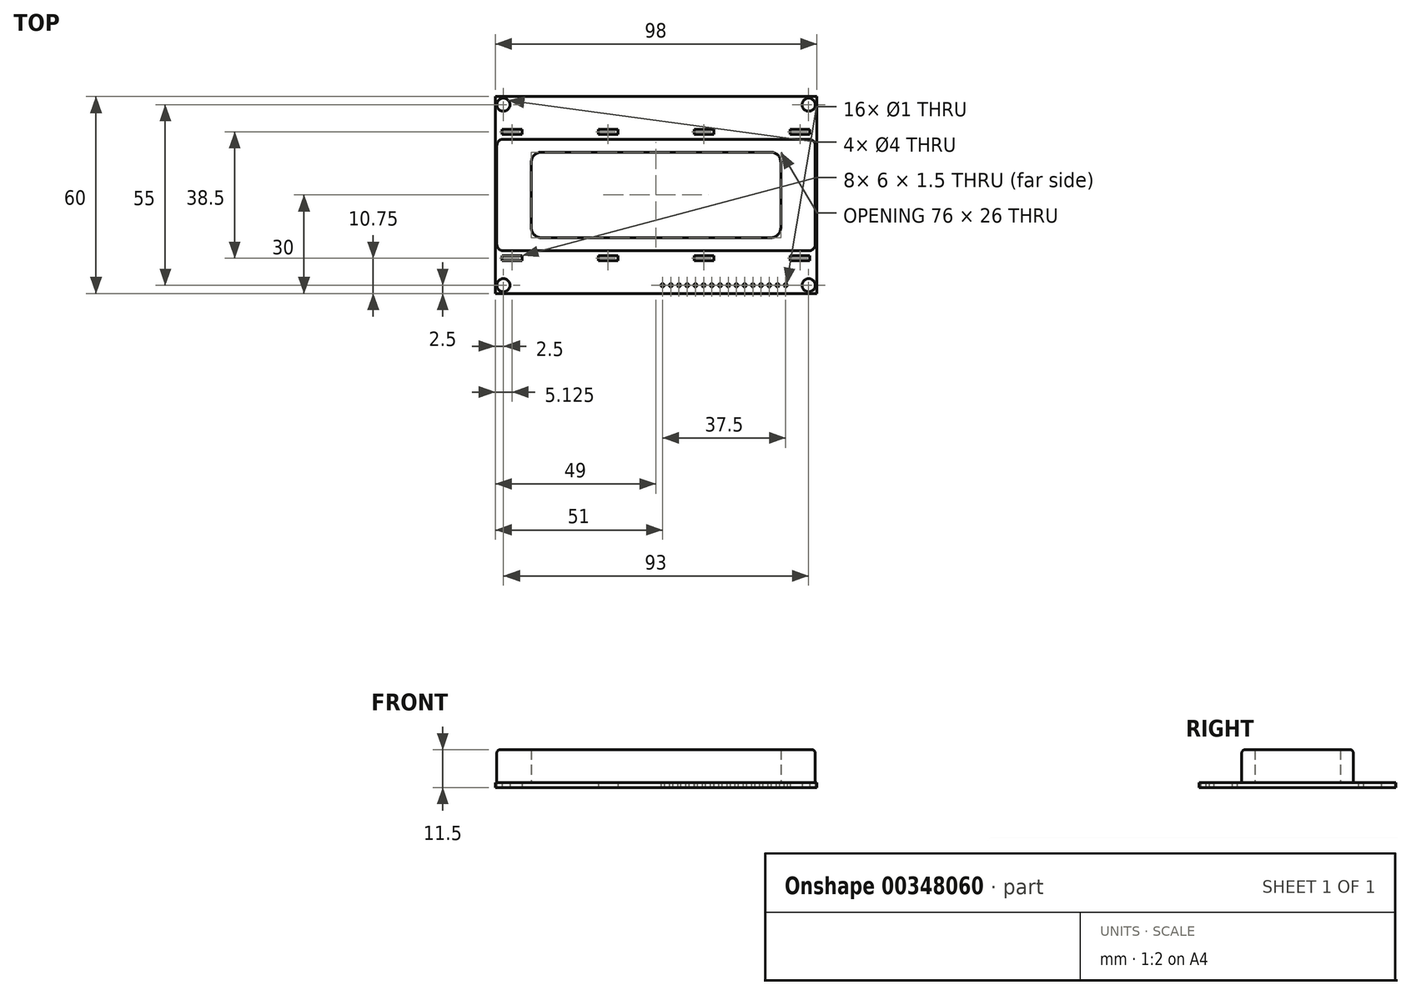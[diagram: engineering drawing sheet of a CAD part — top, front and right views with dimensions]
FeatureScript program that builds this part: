
annotation { "Feature Type Name" : "Feature", "Feature Type Description" : "" }
export const myFeature = defineFeature(function(context is Context, id is Id, definition is map)
    precondition{}
    {
        {
            var Q0;
            Q0=qCreatedBy(makeId("Top.planeOp"),FACE);
            var sketch = newSketch(context, id + "F0", { "sketchPlane" : qUnion([Q0])});
            skLineSegment(sketch, "E0.bottom", {"start": v(-49, 30) * mm, "end": v(49, 30) * mm});
            skLineSegment(sketch, "E0.top", {"start": v(-49, -30) * mm, "end": v(49, -30) * mm});
            skLineSegment(sketch, "E0.left", {"start": v(-49, 30) * mm, "end": v(-49, -30) * mm});
            skLineSegment(sketch, "E0.right", {"start": v(49, 30) * mm, "end": v(49, -30) * mm});
            skPoint(sketch, "E0.middle", {"position": v(0, 0) * mm});
            skCircle(sketch, "E1", {"center": v(-46.5, 27.5) * mm, "radius": 2 * mm});
            skCircle(sketch, "E2.MirrorC", {"center": v(46.5, 27.5) * mm, "radius": 2 * mm});
            skCircle(sketch, "E3.MirrorC", {"center": v(46.5, -27.5) * mm, "radius": 2 * mm});
            skCircle(sketch, "E4.MirrorC", {"center": v(-46.5, -27.5) * mm, "radius": 2 * mm});
            skLineSegment(sketch, "E5.bottom", {"start": v(-46.87, 20) * mm, "end": v(-40.87, 20) * mm});
            skLineSegment(sketch, "E5.top", {"start": v(-46.87, 18.5) * mm, "end": v(-40.87, 18.5) * mm});
            skLineSegment(sketch, "E5.left", {"start": v(-46.87, 20) * mm, "end": v(-46.87, 18.5) * mm});
            skLineSegment(sketch, "E5.right", {"start": v(-40.87, 20) * mm, "end": v(-40.87, 18.5) * mm});
            skLineSegment(sketch, "E6.1.0.0", {"start": v(-17.62, 18.5) * mm, "end": v(-11.62, 18.5) * mm});
            skLineSegment(sketch, "E6.1.0.1", {"start": v(-11.62, 20) * mm, "end": v(-11.62, 18.5) * mm});
            skLineSegment(sketch, "E6.1.0.2", {"start": v(-17.62, 20) * mm, "end": v(-11.62, 20) * mm});
            skLineSegment(sketch, "E6.1.0.3", {"start": v(-17.62, 20) * mm, "end": v(-17.62, 18.5) * mm});
            skLineSegment(sketch, "E6.2.0.0", {"start": v(11.63, 18.5) * mm, "end": v(17.63, 18.5) * mm});
            skLineSegment(sketch, "E6.2.0.1", {"start": v(17.63, 20) * mm, "end": v(17.63, 18.5) * mm});
            skLineSegment(sketch, "E6.2.0.2", {"start": v(11.63, 20) * mm, "end": v(17.63, 20) * mm});
            skLineSegment(sketch, "E6.2.0.3", {"start": v(11.63, 20) * mm, "end": v(11.63, 18.5) * mm});
            skLineSegment(sketch, "E6.3.0.0", {"start": v(40.88, 18.5) * mm, "end": v(46.88, 18.5) * mm});
            skLineSegment(sketch, "E6.3.0.1", {"start": v(46.88, 20) * mm, "end": v(46.88, 18.5) * mm});
            skLineSegment(sketch, "E6.3.0.2", {"start": v(40.88, 20) * mm, "end": v(46.88, 20) * mm});
            skLineSegment(sketch, "E6.3.0.3", {"start": v(40.88, 20) * mm, "end": v(40.88, 18.5) * mm});
            skLineSegment(sketch, "E6.direction1", {"start": v(-46.87, 18.5) * mm, "end": v(-17.62, 18.5) * mm, "construction": true});
            skLineSegment(sketch, "E7.MirrorCS", {"start": v(-46.87, -20) * mm, "end": v(-40.87, -20) * mm});
            skLineSegment(sketch, "E8.MirrorCS", {"start": v(-46.87, -20) * mm, "end": v(-46.87, -18.5) * mm});
            skLineSegment(sketch, "E9.MirrorCS", {"start": v(-40.87, -20) * mm, "end": v(-40.87, -18.5) * mm});
            skLineSegment(sketch, "E10", {"start": v(-46.87, -18.5) * mm, "end": v(-40.87, -18.5) * mm});
            skLineSegment(sketch, "E11.1.0.0", {"start": v(-17.62, -20) * mm, "end": v(-11.62, -20) * mm});
            skLineSegment(sketch, "E11.1.0.1", {"start": v(-17.62, -18.5) * mm, "end": v(-11.62, -18.5) * mm});
            skLineSegment(sketch, "E11.1.0.2", {"start": v(-11.62, -20) * mm, "end": v(-11.62, -18.5) * mm});
            skLineSegment(sketch, "E11.1.0.3", {"start": v(-17.62, -20) * mm, "end": v(-17.62, -18.5) * mm});
            skLineSegment(sketch, "E11.2.0.0", {"start": v(11.63, -20) * mm, "end": v(17.63, -20) * mm});
            skLineSegment(sketch, "E11.2.0.1", {"start": v(11.63, -18.5) * mm, "end": v(17.63, -18.5) * mm});
            skLineSegment(sketch, "E11.2.0.2", {"start": v(17.63, -20) * mm, "end": v(17.63, -18.5) * mm});
            skLineSegment(sketch, "E11.2.0.3", {"start": v(11.63, -20) * mm, "end": v(11.63, -18.5) * mm});
            skLineSegment(sketch, "E11.3.0.0", {"start": v(40.88, -20) * mm, "end": v(46.88, -20) * mm});
            skLineSegment(sketch, "E11.3.0.1", {"start": v(40.88, -18.5) * mm, "end": v(46.88, -18.5) * mm});
            skLineSegment(sketch, "E11.3.0.2", {"start": v(46.88, -20) * mm, "end": v(46.88, -18.5) * mm});
            skLineSegment(sketch, "E11.3.0.3", {"start": v(40.88, -20) * mm, "end": v(40.88, -18.5) * mm});
            skLineSegment(sketch, "E11.direction1", {"start": v(-46.87, -20) * mm, "end": v(-17.62, -20) * mm, "construction": true});
            skCircle(sketch, "E12", {"center": v(2, -27.5) * mm, "radius": 0.5 * mm});
            skCircle(sketch, "E13.1.0.0", {"center": v(4.5, -27.5) * mm, "radius": 0.5 * mm});
            skCircle(sketch, "E13.2.0.0", {"center": v(7, -27.5) * mm, "radius": 0.5 * mm});
            skCircle(sketch, "E13.3.0.0", {"center": v(9.5, -27.5) * mm, "radius": 0.5 * mm});
            skCircle(sketch, "E13.4.0.0", {"center": v(12, -27.5) * mm, "radius": 0.5 * mm});
            skCircle(sketch, "E13.5.0.0", {"center": v(14.5, -27.5) * mm, "radius": 0.5 * mm});
            skCircle(sketch, "E13.6.0.0", {"center": v(17, -27.5) * mm, "radius": 0.5 * mm});
            skCircle(sketch, "E13.7.0.0", {"center": v(19.5, -27.5) * mm, "radius": 0.5 * mm});
            skCircle(sketch, "E13.8.0.0", {"center": v(22, -27.5) * mm, "radius": 0.5 * mm});
            skCircle(sketch, "E13.9.0.0", {"center": v(24.5, -27.5) * mm, "radius": 0.5 * mm});
            skCircle(sketch, "E13.10.0.0", {"center": v(27, -27.5) * mm, "radius": 0.5 * mm});
            skCircle(sketch, "E13.11.0.0", {"center": v(29.5, -27.5) * mm, "radius": 0.5 * mm});
            skCircle(sketch, "E13.12.0.0", {"center": v(32, -27.5) * mm, "radius": 0.5 * mm});
            skCircle(sketch, "E13.13.0.0", {"center": v(34.5, -27.5) * mm, "radius": 0.5 * mm});
            skCircle(sketch, "E13.14.0.0", {"center": v(37, -27.5) * mm, "radius": 0.5 * mm});
            skCircle(sketch, "E13.15.0.0", {"center": v(39.5, -27.5) * mm, "radius": 0.5 * mm});
            skLineSegment(sketch, "E13.direction1", {"start": v(2, -27.5) * mm, "end": v(4.5, -27.5) * mm, "construction": true});
            skSolve(sketch);
        }
        {
            var Q0;
            Q0=makeQuery(id+"F0.imprint","IMPRINT",FACE,{"disambiguationData":[TD([[makeQuery(id+"F0.imprint","IMPRINT",EDGE,{"derivedFrom":sQuery(id+"F0.wireOp",EDGE,"E0.bottom")}),-1.0]])]});
            extrude(context, id + "F1", {"entities" : qUnion([Q0]), "depth" : 1.5 * mm});
        }
        {
            var Q0;
            Q0=makeQuery(id+"F1.opExtrude","CAP_FACE",FACE,{"disambiguationData":[OSD([sQuery(id+"F0.wireOp",EDGE,"E0.bottom"),sQuery(id+"F0.wireOp",EDGE,"E0.top"),sQuery(id+"F0.wireOp",EDGE,"E0.left"),sQuery(id+"F0.wireOp",EDGE,"E0.right"),sQuery(id+"F0.wireOp",EDGE,"E1"),sQuery(id+"F0.wireOp",EDGE,"E2.MirrorC"),sQuery(id+"F0.wireOp",EDGE,"E3.MirrorC"),sQuery(id+"F0.wireOp",EDGE,"E4.MirrorC"),sQuery(id+"F0.wireOp",EDGE,"E5.bottom"),sQuery(id+"F0.wireOp",EDGE,"E5.top"),sQuery(id+"F0.wireOp",EDGE,"E5.left"),sQuery(id+"F0.wireOp",EDGE,"E5.right"),sQuery(id+"F0.wireOp",EDGE,"E6.1.0.0"),sQuery(id+"F0.wireOp",EDGE,"E6.1.0.1"),sQuery(id+"F0.wireOp",EDGE,"E6.1.0.2"),sQuery(id+"F0.wireOp",EDGE,"E6.1.0.3"),sQuery(id+"F0.wireOp",EDGE,"E6.2.0.0"),sQuery(id+"F0.wireOp",EDGE,"E6.2.0.1"),sQuery(id+"F0.wireOp",EDGE,"E6.2.0.2"),sQuery(id+"F0.wireOp",EDGE,"E6.2.0.3"),sQuery(id+"F0.wireOp",EDGE,"E6.3.0.0"),sQuery(id+"F0.wireOp",EDGE,"E6.3.0.1"),sQuery(id+"F0.wireOp",EDGE,"E6.3.0.2"),sQuery(id+"F0.wireOp",EDGE,"E6.3.0.3"),sQuery(id+"F0.wireOp",EDGE,"E7.MirrorCS"),sQuery(id+"F0.wireOp",EDGE,"E8.MirrorCS"),sQuery(id+"F0.wireOp",EDGE,"E9.MirrorCS"),sQuery(id+"F0.wireOp",EDGE,"E10"),sQuery(id+"F0.wireOp",EDGE,"E11.1.0.0"),sQuery(id+"F0.wireOp",EDGE,"E11.1.0.1"),sQuery(id+"F0.wireOp",EDGE,"E11.1.0.2"),sQuery(id+"F0.wireOp",EDGE,"E11.1.0.3"),sQuery(id+"F0.wireOp",EDGE,"E11.2.0.0"),sQuery(id+"F0.wireOp",EDGE,"E11.2.0.1"),sQuery(id+"F0.wireOp",EDGE,"E11.2.0.2"),sQuery(id+"F0.wireOp",EDGE,"E11.2.0.3"),sQuery(id+"F0.wireOp",EDGE,"E11.3.0.0"),sQuery(id+"F0.wireOp",EDGE,"E11.3.0.1"),sQuery(id+"F0.wireOp",EDGE,"E11.3.0.2"),sQuery(id+"F0.wireOp",EDGE,"E11.3.0.3"),sQuery(id+"F0.wireOp",EDGE,"E12"),sQuery(id+"F0.wireOp",EDGE,"E13.1.0.0"),sQuery(id+"F0.wireOp",EDGE,"E13.2.0.0"),sQuery(id+"F0.wireOp",EDGE,"E13.3.0.0"),sQuery(id+"F0.wireOp",EDGE,"E13.4.0.0"),sQuery(id+"F0.wireOp",EDGE,"E13.5.0.0"),sQuery(id+"F0.wireOp",EDGE,"E13.6.0.0"),sQuery(id+"F0.wireOp",EDGE,"E13.7.0.0"),sQuery(id+"F0.wireOp",EDGE,"E13.8.0.0"),sQuery(id+"F0.wireOp",EDGE,"E13.9.0.0"),sQuery(id+"F0.wireOp",EDGE,"E13.10.0.0"),sQuery(id+"F0.wireOp",EDGE,"E13.11.0.0"),sQuery(id+"F0.wireOp",EDGE,"E13.12.0.0"),sQuery(id+"F0.wireOp",EDGE,"E13.13.0.0"),sQuery(id+"F0.wireOp",EDGE,"E13.14.0.0"),sQuery(id+"F0.wireOp",EDGE,"E13.15.0.0")])],"isStart":false});
            var sketch = newSketch(context, id + "F2", { "sketchPlane" : qUnion([Q0])});
            skLineSegment(sketch, "E14.bottom", {"start": v(-46.5, 17) * mm, "end": v(46.5, 17) * mm});
            skLineSegment(sketch, "E14.top", {"start": v(-46.5, -17) * mm, "end": v(46.5, -17) * mm});
            skLineSegment(sketch, "E14.left", {"start": v(-48.5, 15) * mm, "end": v(-48.5, -15) * mm});
            skLineSegment(sketch, "E14.right", {"start": v(48.5, 15) * mm, "end": v(48.5, -15) * mm});
            skPoint(sketch, "E14.middle", {"position": v(0, 0) * mm});
            skLineSegment(sketch, "E15.bottom", {"start": v(-35, 13) * mm, "end": v(35, 13) * mm});
            skLineSegment(sketch, "E15.top", {"start": v(-35, -13) * mm, "end": v(35, -13) * mm});
            skLineSegment(sketch, "E15.left", {"start": v(-38, 10) * mm, "end": v(-38, -10) * mm});
            skLineSegment(sketch, "E15.right", {"start": v(38, 10) * mm, "end": v(38, -10) * mm});
            skPoint(sketch, "E16.visualSharp", {"position": v(-38, 13) * mm});
            skArc(sketch, "E16.filletArc", {"start": v(-35, 13) * mm, "mid": v(-37.12, 12.12) * mm, "end": v(-38, 10) * mm});
            skPoint(sketch, "E17.visualSharp", {"position": v(-38, -13) * mm});
            skArc(sketch, "E17.filletArc", {"start": v(-38, -10) * mm, "mid": v(-37.12, -12.12) * mm, "end": v(-35, -13) * mm});
            skPoint(sketch, "E18.visualSharp", {"position": v(38, -13) * mm});
            skArc(sketch, "E18.filletArc", {"start": v(35, -13) * mm, "mid": v(37.12, -12.12) * mm, "end": v(38, -10) * mm});
            skPoint(sketch, "E19.visualSharp", {"position": v(38, 13) * mm});
            skArc(sketch, "E19.filletArc", {"start": v(38, 10) * mm, "mid": v(37.12, 12.12) * mm, "end": v(35, 13) * mm});
            skPoint(sketch, "E20.visualSharp", {"position": v(-48.5, 17) * mm});
            skArc(sketch, "E20.filletArc", {"start": v(-46.5, 17) * mm, "mid": v(-47.91, 16.41) * mm, "end": v(-48.5, 15) * mm});
            skPoint(sketch, "E21.visualSharp", {"position": v(-48.5, -17) * mm});
            skArc(sketch, "E21.filletArc", {"start": v(-48.5, -15) * mm, "mid": v(-47.91, -16.41) * mm, "end": v(-46.5, -17) * mm});
            skPoint(sketch, "E22.visualSharp", {"position": v(48.5, 17) * mm});
            skArc(sketch, "E22.filletArc", {"start": v(48.5, 15) * mm, "mid": v(47.91, 16.41) * mm, "end": v(46.5, 17) * mm});
            skPoint(sketch, "E23.visualSharp", {"position": v(48.5, -17) * mm});
            skArc(sketch, "E23.filletArc", {"start": v(46.5, -17) * mm, "mid": v(47.91, -16.41) * mm, "end": v(48.5, -15) * mm});
            skSolve(sketch);
        }
        {
            var Q0;
            Q0=makeQuery(id+"F2.imprint","IMPRINT",FACE,{"disambiguationData":[TD([[makeQuery(id+"F2.imprint","IMPRINT",EDGE,{"derivedFrom":sQuery(id+"F2.wireOp",EDGE,"E14.bottom")}),-1.0]])]});
            extrude(context, id + "F3", {"entities" : qUnion([Q0]), "depth" : 10 * mm});
        }
        {
            var Q0;
            Q0=makeQuery(id+"F2.imprint","IMPRINT",FACE,{"disambiguationData":[TD([[makeQuery(id+"F2.imprint","IMPRINT",EDGE,{"derivedFrom":sQuery(id+"F2.wireOp",EDGE,"E15.bottom")}),-1.0]])]});
            extrude(context, id + "F4", {"entities" : qUnion([Q0]), "depth" : 10 * mm});
        }
        {
            var Q0;
            Q0=makeQuery(id+"F3.opExtrude","CAP_EDGE",EDGE,{"disambiguationData":[OSD([sQuery(id+"F2.wireOp",EDGE,"E14.top")])],"isStart":false});
            fillet(context, id + "F5", {"entities" : qUnion([Q0]), "radius" : 1 * mm, "tangentPropagation" : true, "allowEdgeOverflow" : false});
        }
    });
